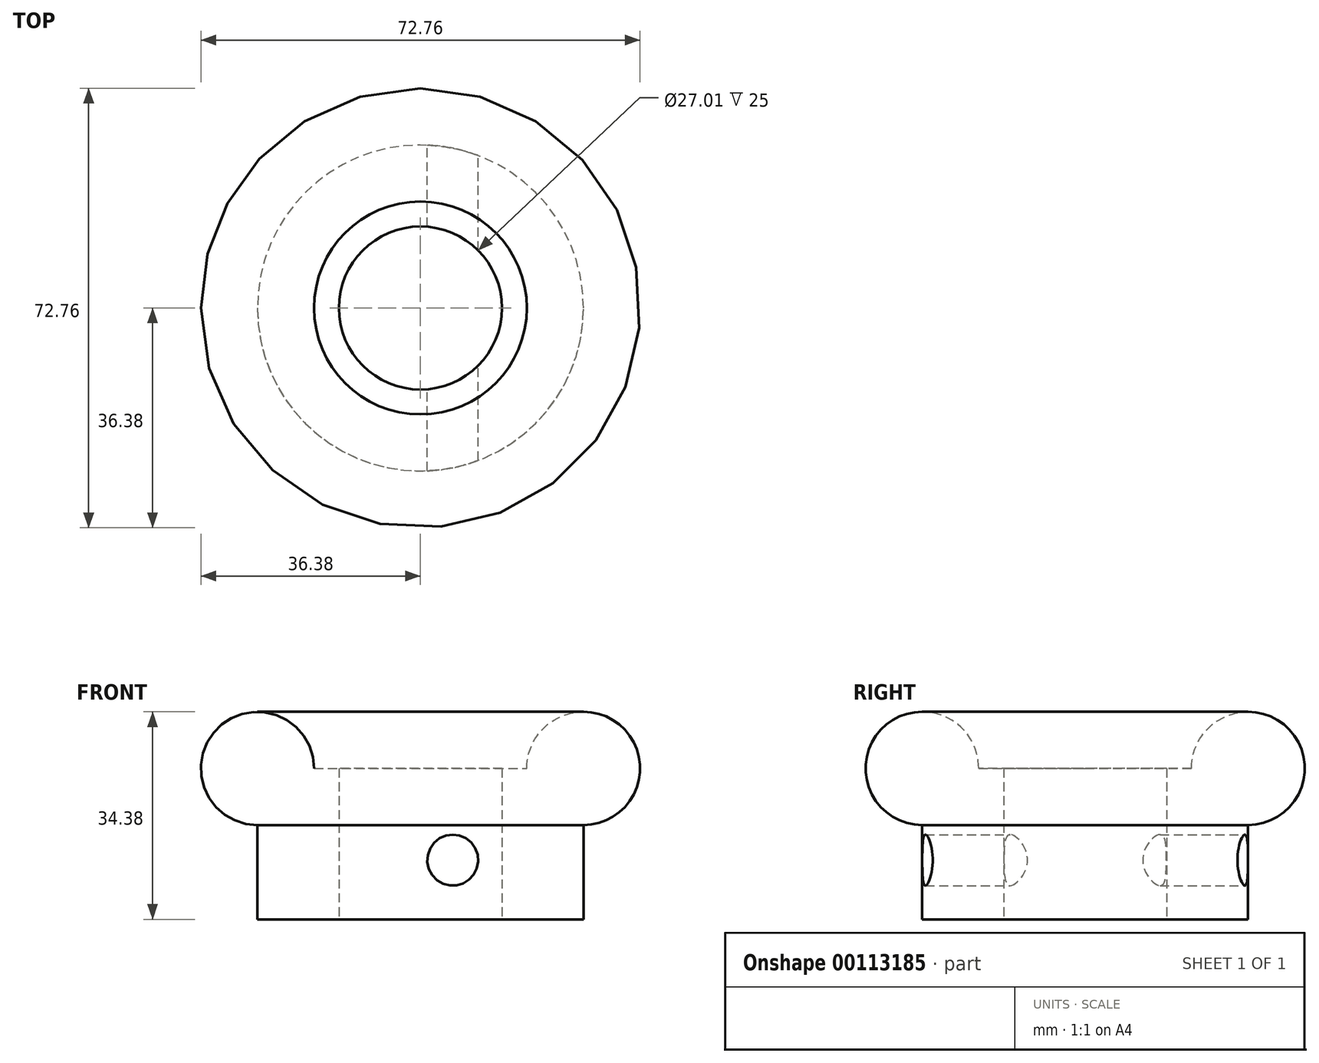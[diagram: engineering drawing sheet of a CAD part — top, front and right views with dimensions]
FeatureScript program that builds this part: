
annotation { "Feature Type Name" : "Feature", "Feature Type Description" : "" }
export const myFeature = defineFeature(function(context is Context, id is Id, definition is map)
    precondition{}
    {
        {
            var Q0;
            Q0=qCreatedBy(makeId("Top.planeOp"),FACE);
            var sketch = newSketch(context, id + "F0", { "sketchPlane" : qUnion([Q0])});
            skCircle(sketch, "E0", {"center": v(0, 0) * mm, "radius": 27 * mm});
            skCircle(sketch, "E1", {"center": v(0, 0) * mm, "radius": 13.5 * mm});
            skSolve(sketch);
        }
        {
            var Q0;
            Q0 = qSketchRegion(id + "F0", true);
            extrude(context, id + "F1", {"entities" : qUnion([Q0]), "depth" : 25 * mm});
        }
        {
            var Q0;
            Q0=qCreatedBy(makeId("Right.planeOp"),FACE);
            var sketch = newSketch(context, id + "F2", { "sketchPlane" : qUnion([Q0])});
            skCircle(sketch, "E2", {"center": v(-27, 25) * mm, "radius": 9.38 * mm});
            skSolve(sketch);
        }
        {
            var Q0;
            Q0=makeQuery(id+"F2.imprint","IMPRINT",FACE,{"disambiguationData":[TD([[makeQuery(id+"F2.imprint","IMPRINT",EDGE,{"derivedFrom":sQuery(id+"F2.wireOp",EDGE,"E2")}),1.0]])]});
            var Q1;
            Q1=makeQuery(id+"F1.opExtrude","SWEPT_FACE",FACE,{"disambiguationData":[OSD([sQuery(id+"F0.wireOp",EDGE,"E1")])]});
            revolve(context, id + "F3", {"operationType" : NewBodyOperationType.ADD, "entities" : qUnion([Q0]), "axis" : qUnion([Q1]), "revolveType" : RevolveType.FULL});
        }
        {
            var Q0;
            Q0=qCreatedBy(makeId("Front.planeOp"),FACE);
            var sketch = newSketch(context, id + "F4", { "sketchPlane" : qUnion([Q0])});
            skCircle(sketch, "E3", {"center": v(5.35, 9.81) * mm, "radius": 4.22 * mm});
            skSolve(sketch);
        }
        {
            var Q0;
            Q0=makeQuery(id+"F4.imprint","IMPRINT",FACE,{"disambiguationData":[TD([[makeQuery(id+"F4.imprint","IMPRINT",EDGE,{"derivedFrom":sQuery(id+"F4.wireOp",EDGE,"E3")}),1.0]])]});
            var Q1;
            Q1=sQuery(id+"F4.wireOp",EDGE,"E3");
            extrude(context, id + "F5", {"entities" : qUnion([Q0]), "operationType" : NewBodyOperationType.REMOVE, "surfaceEntities" : qUnion([Q1]), "depth" : 30 * mm, "hasSecondDirection" : true, "secondDirectionOppositeDirection" : true, "secondDirectionDepth" : 30 * mm});
        }
    });
